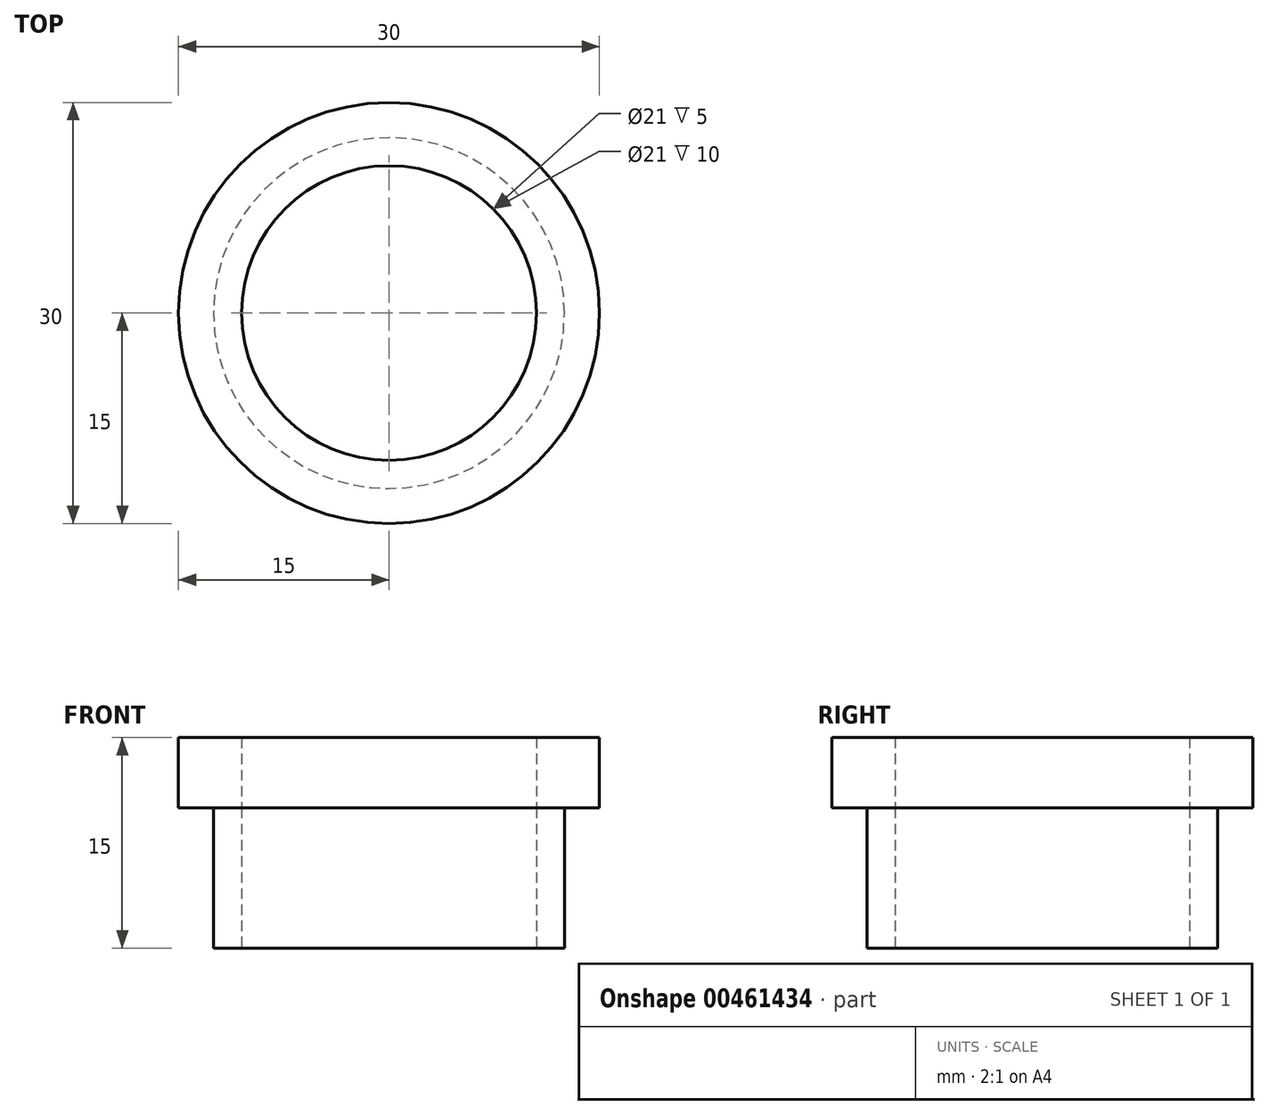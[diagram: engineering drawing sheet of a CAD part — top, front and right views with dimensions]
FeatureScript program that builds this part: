
annotation { "Feature Type Name" : "Feature", "Feature Type Description" : "" }
export const myFeature = defineFeature(function(context is Context, id is Id, definition is map)
    precondition{}
    {
        {
            var Q0;
            Q0=qCreatedBy(makeId("Top.planeOp"),FACE);
            var sketch = newSketch(context, id + "F0", { "sketchPlane" : qUnion([Q0])});
            skCircle(sketch, "E0", {"center": v(0, 0) * mm, "radius": 12.5 * mm});
            skSolve(sketch);
        }
        {
            var Q0;
            Q0 = qSketchRegion(id + "F0", true);
            extrude(context, id + "F1", {"entities" : qUnion([Q0]), "depth" : 10 * mm});
        }
        {
            var Q0;
            Q0=makeQuery(id+"F1.opExtrude","CAP_FACE",FACE,{"disambiguationData":[OSD([sQuery(id+"F0.wireOp",EDGE,"E0")])],"isStart":false});
            var sketch = newSketch(context, id + "F2", { "sketchPlane" : qUnion([Q0])});
            skCircle(sketch, "E1", {"center": v(0, 0) * mm, "radius": 15 * mm});
            skSolve(sketch);
        }
        {
            var Q0;
            Q0=makeQuery(id+"F2.imprint","IMPRINT",FACE,{"disambiguationData":[TD([[makeQuery(id+"F2.imprint","IMPRINT",EDGE,{"derivedFrom":sQuery(id+"F2.wireOp",EDGE,"E1")}),1.0]])]});
            var Q1;
            Q1=makeQuery(id+"F2.imprint","IMPRINT",FACE,{"disambiguationData":[TD([[makeQuery(id+"F2.imprint","IMPRINT",EDGE,{"derivedFrom":makeQuery(id+"F1.opExtrude","CAP_EDGE",EDGE,{"disambiguationData":[OSD([sQuery(id+"F0.wireOp",EDGE,"E0")])],"isStart":false})}),1.0]])]});
            extrude(context, id + "F3", {"entities" : qUnion([Q0, Q1]), "depth" : 5 * mm});
        }
        {
            var Q0;
            Q0=makeQuery(id+"F1.opExtrude","CAP_FACE",FACE,{"disambiguationData":[OSD([sQuery(id+"F0.wireOp",EDGE,"E0")])],"isStart":true});
            var sketch = newSketch(context, id + "F4", { "sketchPlane" : qUnion([Q0])});
            skCircle(sketch, "E2", {"center": v(0, 0) * mm, "radius": 10.5 * mm});
            skSolve(sketch);
        }
        {
            var Q0;
            Q0=makeQuery(id+"F4.imprint","IMPRINT",FACE,{"disambiguationData":[TD([[makeQuery(id+"F4.imprint","IMPRINT",EDGE,{"derivedFrom":sQuery(id+"F4.wireOp",EDGE,"E2")}),1.0]])]});
            var Q1;
            Q1=sQuery(id+"F4.wireOp",EDGE,"E2");
            extrude(context, id + "F5", {"entities" : qUnion([Q0]), "operationType" : NewBodyOperationType.REMOVE, "surfaceEntities" : qUnion([Q1]), "oppositeDirection" : true, "depth" : 50.6 * mm});
        }
    });
